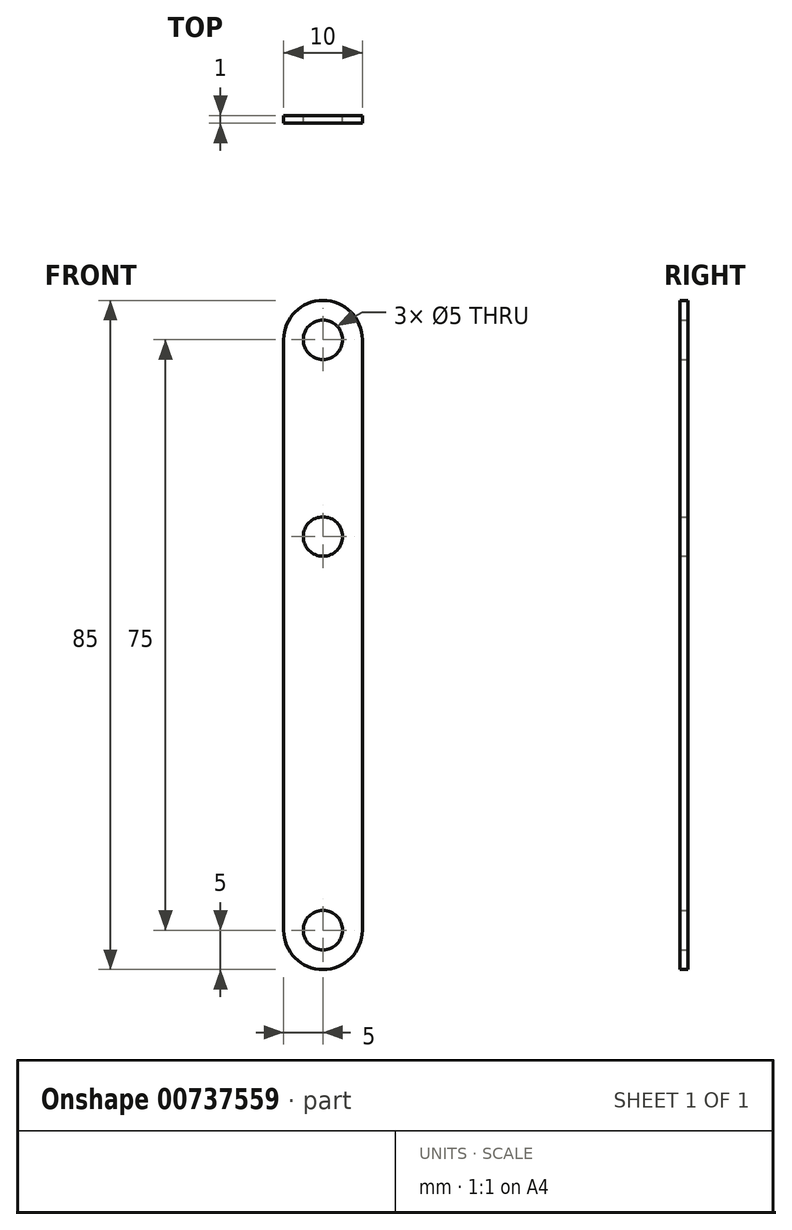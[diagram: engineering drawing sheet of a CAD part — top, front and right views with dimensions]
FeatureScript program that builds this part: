
annotation { "Feature Type Name" : "Feature", "Feature Type Description" : "" }
export const myFeature = defineFeature(function(context is Context, id is Id, definition is map)
    precondition{}
    {
        {
            var Q0;
            Q0=qCreatedBy(makeId("Front.planeOp"),FACE);
            var sketch = newSketch(context, id + "F0", { "sketchPlane" : qUnion([Q0])});
            skArc(sketch, "E0", {"start": v(-5, -50) * mm, "mid": v(0, -55) * mm, "end": v(5, -50) * mm});
            skArc(sketch, "E1", {"start": v(5, 25) * mm, "mid": v(0, 30) * mm, "end": v(-5, 25) * mm});
            skCircle(sketch, "E2", {"center": v(0, 0) * mm, "radius": 2.5 * mm});
            skLineSegment(sketch, "E3", {"start": v(-5, 25) * mm, "end": v(-5, -50) * mm});
            skLineSegment(sketch, "E4", {"start": v(5, 25) * mm, "end": v(5, -50) * mm});
            skCircle(sketch, "E5", {"center": v(0, 25) * mm, "radius": 2.5 * mm});
            skCircle(sketch, "E6", {"center": v(0, -50) * mm, "radius": 2.5 * mm});
            skSolve(sketch);
        }
        {
            var Q0;
            Q0 = qSketchRegion(id + "F0", true);
            extrude(context, id + "F1", {"entities" : qUnion([Q0]), "depth" : 1 * mm, "offsetDistance" : 25 * mm});
        }
    });
